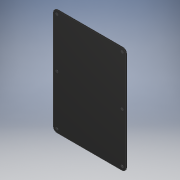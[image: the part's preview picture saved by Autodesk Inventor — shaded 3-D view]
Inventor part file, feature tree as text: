
AUTODESK INVENTOR PART (.ipt)
format: ipt  version: 2019 (Build 230136000, 136)  size: 549,376 bytes
history: native  units: in
note: dims shown in document units (in); Inventor stores cm internally (conversion verified against a paired STEP export)
features: other x2, extrude x1, sketch x1
ambient origin geometry x8: Origin, YZ Plane, XZ Plane, XY Plane, X Axis, Y Axis, Z Axis, Center Point
bodies: Solid1 (feature_tree)
feature tree (4):
  other  "LID"
  other  "MeshFeature1"
  extrude  "Extrusion1"  [1 undecoded]
  sketch  "Sketch1"  dims[d0=1.0in d1=0.0in]
note: 1 required parameter value undecoded (feature->parameter linkage not recoverable at this tier; creation-order binding heuristic only, values carry confidence <= 0.55)
